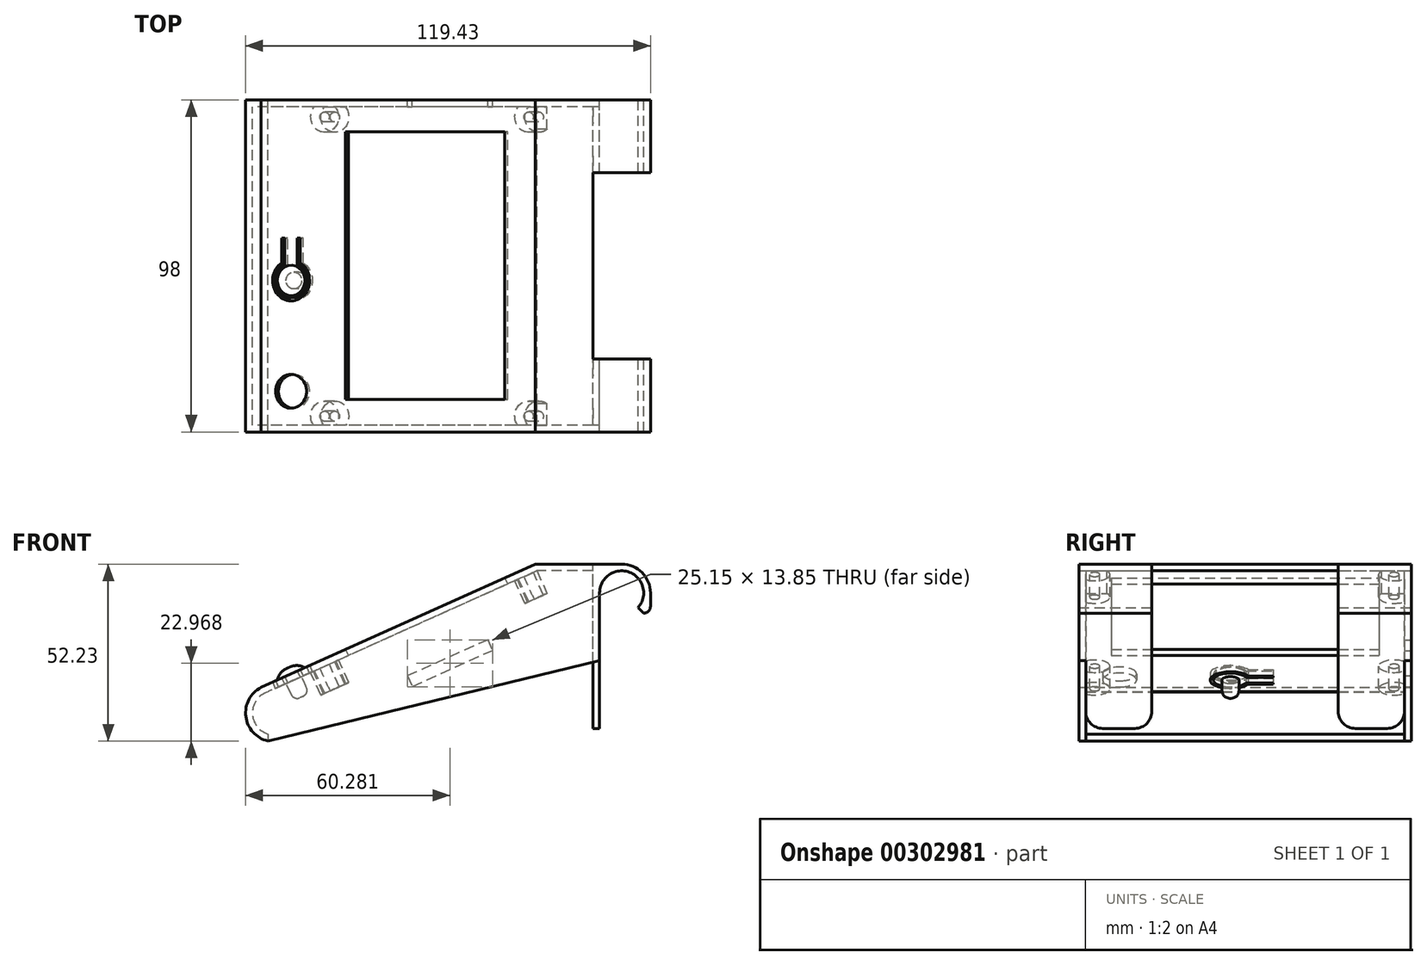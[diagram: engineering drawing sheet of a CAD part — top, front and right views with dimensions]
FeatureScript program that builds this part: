
annotation { "Feature Type Name" : "Feature", "Feature Type Description" : "" }
export const myFeature = defineFeature(function(context is Context, id is Id, definition is map)
    precondition{}
    {
        {
            var Q0;
            Q0=qCreatedBy(makeId("Front.planeOp"),FACE);
            var sketch = newSketch(context, id + "F0", { "sketchPlane" : qUnion([Q0])});
            skLineSegment(sketch, "E0", {"start": v(0, 0) * mm, "end": v(0, -42.85) * mm, "construction": true});
            skLineSegment(sketch, "E1", {"start": v(0, -42.85) * mm, "end": v(-104.35, -42.85) * mm, "construction": true});
            skLineSegment(sketch, "E2", {"start": v(-8.5, 6.5) * mm, "end": v(-25, 6.5) * mm});
            skLineSegment(sketch, "E3", {"start": v(-25, 6.5) * mm, "end": v(-104.35, -29.17) * mm});
            skLineSegment(sketch, "E4", {"start": v(-104.35, -29.17) * mm, "end": v(-104.35, -29.2) * mm});
            skLineSegment(sketch, "E5", {"start": v(-104.35, -29.17) * mm, "end": v(-98.2, -42.85) * mm, "construction": true});
            skLineSegment(sketch, "E6", {"start": v(-25, 6.5) * mm, "end": v(-18.85, -7.18) * mm, "construction": true});
            skLineSegment(sketch, "E7", {"start": v(-6.5, 0) * mm, "end": v(-6.5, -20) * mm});
            skArc(sketch, "E8.0", {"start": v(8.5, 0) * mm, "mid": v(6.01, 6.01) * mm, "end": v(0, 8.5) * mm});
            skLineSegment(sketch, "E9.1", {"start": v(-25.43, 8.5) * mm, "end": v(-106.35, -27.87) * mm});
            skLineSegment(sketch, "E9.2", {"start": v(0, 8.5) * mm, "end": v(-25.43, 8.5) * mm});
            skLineSegment(sketch, "E10", {"start": v(8.5, 0) * mm, "end": v(8.5, -6) * mm});
            skLineSegment(sketch, "E11", {"start": v(8.5, -6) * mm, "end": v(6.5, -6) * mm});
            skLineSegment(sketch, "E12", {"start": v(-8.5, 0) * mm, "end": v(-8.5, -20) * mm});
            skLineSegment(sketch, "E13", {"start": v(-8.5, -20) * mm, "end": v(-6.5, -20) * mm});
            skLineSegment(sketch, "E14", {"start": v(-8.5, 0) * mm, "end": v(-8.5, 6.5) * mm});
            skPoint(sketch, "E15.orphan", {"position": v(0, 6.5) * mm});
            skArc(sketch, "E16", {"start": v(-105.43, -27.46) * mm, "mid": v(-110.9, -36) * mm, "end": v(-104.35, -43.73) * mm});
            skPoint(sketch, "E16.third.point", {"position": v(-95.6, -40.58) * mm});
            skArc(sketch, "E17.0", {"start": v(-104.34, -29.2) * mm, "mid": v(-108.93, -35.42) * mm, "end": v(-104.35, -41.66) * mm});
            skLineSegment(sketch, "E18.trimOffspring", {"start": v(-104.35, -41.66) * mm, "end": v(-104.35, -42.85) * mm});
            skLineSegment(sketch, "E19", {"start": v(-104.35, -42.85) * mm, "end": v(-104.35, -43.73) * mm});
            skArc(sketch, "E20", {"start": v(4.85, -4.33) * mm, "mid": v(2.32, 6.07) * mm, "end": v(-6.5, 0) * mm});
            skLineSegment(sketch, "E21", {"start": v(6.5, -6) * mm, "end": v(4.85, -4.33) * mm});
            skSolve(sketch);
        }
        {
            var Q0;
            Q0=makeQuery(id+"F0.imprint","IMPRINT",FACE,{"disambiguationData":[TD([[makeQuery(id+"F0.imprint","IMPRINT",EDGE,{"derivedFrom":sQuery(id+"F0.wireOp",EDGE,"BKP1fskQ-plHT-HgYq-gCD3-4WAbrrdzwZiy")}),-1.0]])]});
            var Q1;
            Q1=makeQuery(id+"F0.imprint","IMPRINT",FACE,{"disambiguationData":[TD([[makeQuery(id+"F0.imprint","IMPRINT",EDGE,{"derivedFrom":sQuery(id+"F0.wireOp",EDGE,"E2")}),-1.0]])]});
            extrude(context, id + "F1", {"entities" : qUnion([Q0, Q1]), "endBound" : BoundingType.SYMMETRIC, "depth" : 98 * mm, "offsetDistance" : 25 * mm});
        }
        {
            var Q0;
            Q0=makeQuery(id+"F1.opExtrude","SWEPT_FACE",FACE,{"disambiguationData":[OSD([sQuery(id+"F0.wireOp",EDGE,"E3")])]});
            var sketch = newSketch(context, id + "F2", { "sketchPlane" : qUnion([Q0])});
            skLineSegment(sketch, "E22", {"start": v(-20.14, 44.35) * mm, "end": v(-22.79, 44.35) * mm, "construction": true});
            skCircle(sketch, "E23", {"center": v(-22.79, 44.35) * mm, "radius": 1.5 * mm});
            skCircle(sketch, "E24", {"center": v(-22.79, 44.35) * mm, "radius": 4.5 * mm});
            skLineSegment(sketch, "E25", {"start": v(-22.79, 44.35) * mm, "end": v(-22.79, -43.95) * mm, "construction": true});
            skCircle(sketch, "E26", {"center": v(-22.79, -43.95) * mm, "radius": 1.5 * mm});
            skCircle(sketch, "E27", {"center": v(-22.79, -43.95) * mm, "radius": 4.5 * mm});
            skLineSegment(sketch, "E28", {"start": v(-22.79, 44.35) * mm, "end": v(-88.79, 44.35) * mm, "construction": true});
            skCircle(sketch, "E29", {"center": v(-88.79, 44.35) * mm, "radius": 1.5 * mm});
            skCircle(sketch, "E30", {"center": v(-88.79, 44.35) * mm, "radius": 4.5 * mm});
            skLineSegment(sketch, "E31", {"start": v(-88.79, 44.35) * mm, "end": v(-88.79, -43.95) * mm, "construction": true});
            skCircle(sketch, "E32", {"center": v(-88.79, -43.95) * mm, "radius": 1.5 * mm});
            skCircle(sketch, "E33", {"center": v(-88.79, -43.95) * mm, "radius": 4.5 * mm});
            skLineSegment(sketch, "E34", {"start": v(-20.14, 39.4) * mm, "end": v(-29.64, 39.4) * mm, "construction": true});
            skLineSegment(sketch, "E35.bottom", {"start": v(-29.64, 39.4) * mm, "end": v(-81.14, 39.4) * mm});
            skLineSegment(sketch, "E35.top", {"start": v(-29.64, -39.6) * mm, "end": v(-81.14, -39.6) * mm});
            skLineSegment(sketch, "E35.left", {"start": v(-29.64, 39.4) * mm, "end": v(-29.64, -39.6) * mm});
            skLineSegment(sketch, "E35.right", {"start": v(-81.14, 39.4) * mm, "end": v(-81.14, -39.6) * mm});
            skLineSegment(sketch, "E36", {"start": v(-98.75, 49) * mm, "end": v(-98.75, 37) * mm, "construction": true});
            skCircle(sketch, "E37", {"center": v(-98.75, 37) * mm, "radius": 5 * mm});
            skLineSegment(sketch, "E38", {"start": v(-98.75, 37) * mm, "end": v(-98.75, 4.3) * mm, "construction": true});
            skArc(sketch, "E39", {"start": v(-96.75, -0.28) * mm, "mid": v(-98.75, 9.3) * mm, "end": v(-100.75, -0.28) * mm});
            skArc(sketch, "E40", {"start": v(-95.75, -0.9) * mm, "mid": v(-98.75, 10.3) * mm, "end": v(-101.75, -0.9) * mm});
            skLineSegment(sketch, "E41", {"start": v(-98.75, 9.82) * mm, "end": v(-98.75, 4.3) * mm, "construction": true});
            skLineSegment(sketch, "E42", {"start": v(-100.75, -0.28) * mm, "end": v(-100.75, -8.28) * mm});
            skLineSegment(sketch, "E43", {"start": v(-96.75, -0.28) * mm, "end": v(-96.75, -8.28) * mm});
            skLineSegment(sketch, "E44", {"start": v(-101.75, -0.9) * mm, "end": v(-101.75, -8.28) * mm});
            skLineSegment(sketch, "E45", {"start": v(-95.75, -0.9) * mm, "end": v(-95.75, -8.28) * mm});
            skLineSegment(sketch, "E46", {"start": v(-95.75, -8.28) * mm, "end": v(-96.75, -8.28) * mm});
            skLineSegment(sketch, "E47", {"start": v(-100.75, -8.28) * mm, "end": v(-101.75, -8.28) * mm});
            skSolve(sketch);
        }
        {
            var Q0;
            Q0=makeQuery(id+"F2.imprint","IMPRINT",FACE,{"disambiguationData":[TD([[makeQuery(id+"F2.imprint","IMPRINT",EDGE,{"derivedFrom":sQuery(id+"F2.wireOp",EDGE,"FYazuGxI-XyyZ-jJ84-9QZj-pF02LvgmxLtU")}),1.0]])]});
            var Q1;
            Q1=makeQuery(id+"F2.imprint","IMPRINT",FACE,{"disambiguationData":[TD([[makeQuery(id+"F2.imprint","IMPRINT",EDGE,{"derivedFrom":sQuery(id+"F2.wireOp",EDGE,"E35.bottom")}),1.0]])]});
            extrude(context, id + "F3", {"entities" : qUnion([Q0, Q1]), "operationType" : NewBodyOperationType.REMOVE, "oppositeDirection" : true, "depth" : 2 * mm, "offsetDistance" : 25 * mm});
        }
        {
            var Q0;
            Q0=makeQuery(id+"F2.imprint","IMPRINT",FACE,{"disambiguationData":[TD([[makeQuery(id+"F2.imprint","IMPRINT",EDGE,{"derivedFrom":sQuery(id+"F2.wireOp",EDGE,"E23")}),-1.0]])]});
            var Q1;
            Q1=makeQuery(id+"F2.imprint","IMPRINT",FACE,{"disambiguationData":[TD([[makeQuery(id+"F2.imprint","IMPRINT",EDGE,{"derivedFrom":sQuery(id+"F2.wireOp",EDGE,"E26")}),-1.0]])]});
            var Q2;
            Q2=makeQuery(id+"F2.imprint","IMPRINT",FACE,{"disambiguationData":[TD([[makeQuery(id+"F2.imprint","IMPRINT",EDGE,{"derivedFrom":sQuery(id+"F2.wireOp",EDGE,"E32")}),-1.0]])]});
            var Q3;
            Q3=makeQuery(id+"F2.imprint","IMPRINT",FACE,{"disambiguationData":[TD([[makeQuery(id+"F2.imprint","IMPRINT",EDGE,{"derivedFrom":sQuery(id+"F2.wireOp",EDGE,"E29")}),-1.0]])]});
            extrude(context, id + "F4", {"entities" : qUnion([Q0, Q1, Q2, Q3]), "operationType" : NewBodyOperationType.ADD, "depth" : 7.3 * mm, "offsetDistance" : 25 * mm});
        }
        {
            var Q0;
            Q0=makeQuery(id+"F1.opExtrude","CAP_FACE",FACE,{"disambiguationData":[OSD([sQuery(id+"F0.wireOp",EDGE,"BKP1fskQ-plHT-HgYq-gCD3-4WAbrrdzwZiy"),sQuery(id+"F0.wireOp",EDGE,"E2"),sQuery(id+"F0.wireOp",EDGE,"E3"),sQuery(id+"F0.wireOp",EDGE,"E4"),sQuery(id+"F0.wireOp",EDGE,"KLzS8VjV-iBDu-Stew-j29a-tq2aAh7S9TWP"),sQuery(id+"F0.wireOp",EDGE,"E7"),sQuery(id+"F0.wireOp",EDGE,"E8.0"),sQuery(id+"F0.wireOp",EDGE,"E9.1"),sQuery(id+"F0.wireOp",EDGE,"E9.2"),sQuery(id+"F0.wireOp",EDGE,"E10"),sQuery(id+"F0.wireOp",EDGE,"E11"),sQuery(id+"F0.wireOp",EDGE,"E12"),sQuery(id+"F0.wireOp",EDGE,"E13"),sQuery(id+"F0.wireOp",EDGE,"E14"),sQuery(id+"F0.wireOp",EDGE,"E16"),sQuery(id+"F0.wireOp",EDGE,"E17.0"),sQuery(id+"F0.wireOp",EDGE,"E18.trimOffspring"),sQuery(id+"F0.wireOp",EDGE,"E19")])],"isStart":false});
            var sketch = newSketch(context, id + "F5", { "sketchPlane" : qUnion([Q0])});
            skLineSegment(sketch, "E48", {"start": v(-6.5, -20) * mm, "end": v(-104.35, -43.73) * mm});
            skSolve(sketch);
        }
        {
            var Q0;
            Q0=makeQuery(id+"F5.imprint","IMPRINT",FACE,{"disambiguationData":[TD([[makeQuery(id+"F5.imprint","IMPRINT",EDGE,{"derivedFrom":sQuery(id+"F5.wireOp",EDGE,"E48")}),-1.0]])]});
            extrude(context, id + "F6", {"entities" : qUnion([Q0]), "operationType" : NewBodyOperationType.ADD, "oppositeDirection" : true, "depth" : 2 * mm, "offsetDistance" : 25 * mm});
        }
        {
            var Q0;
            Q0=makeQuery(id+"F1.opExtrude","CAP_FACE",FACE,{"disambiguationData":[OSD([sQuery(id+"F0.wireOp",EDGE,"BKP1fskQ-plHT-HgYq-gCD3-4WAbrrdzwZiy"),sQuery(id+"F0.wireOp",EDGE,"E2"),sQuery(id+"F0.wireOp",EDGE,"E3"),sQuery(id+"F0.wireOp",EDGE,"E4"),sQuery(id+"F0.wireOp",EDGE,"KLzS8VjV-iBDu-Stew-j29a-tq2aAh7S9TWP"),sQuery(id+"F0.wireOp",EDGE,"E7"),sQuery(id+"F0.wireOp",EDGE,"E8.0"),sQuery(id+"F0.wireOp",EDGE,"E9.1"),sQuery(id+"F0.wireOp",EDGE,"E9.2"),sQuery(id+"F0.wireOp",EDGE,"E10"),sQuery(id+"F0.wireOp",EDGE,"E11"),sQuery(id+"F0.wireOp",EDGE,"E12"),sQuery(id+"F0.wireOp",EDGE,"E13"),sQuery(id+"F0.wireOp",EDGE,"E14"),sQuery(id+"F0.wireOp",EDGE,"E16"),sQuery(id+"F0.wireOp",EDGE,"E17.0"),sQuery(id+"F0.wireOp",EDGE,"E18.trimOffspring"),sQuery(id+"F0.wireOp",EDGE,"E19")])],"isStart":true});
            var sketch = newSketch(context, id + "F7", { "sketchPlane" : qUnion([Q0])});
            skLineSegment(sketch, "E49", {"start": v(6.5, -20) * mm, "end": v(104.35, -43.73) * mm});
            skSolve(sketch);
        }
        {
            var Q0;
            Q0=makeQuery(id+"F7.imprint","IMPRINT",FACE,{"disambiguationData":[TD([[makeQuery(id+"F7.imprint","IMPRINT",EDGE,{"derivedFrom":sQuery(id+"F7.wireOp",EDGE,"E49")}),1.0]])]});
            extrude(context, id + "F8", {"entities" : qUnion([Q0]), "operationType" : NewBodyOperationType.ADD, "oppositeDirection" : true, "depth" : 2 * mm, "offsetDistance" : 25 * mm});
        }
        {
            var Q0;
            Q0=makeQuery(id+"F2.imprint","IMPRINT",FACE,{"disambiguationData":[TD([[makeQuery(id+"F2.imprint","IMPRINT",EDGE,{"derivedFrom":sQuery(id+"F2.wireOp",EDGE,"E37")}),1.0]])]});
            extrude(context, id + "F9", {"entities" : qUnion([Q0]), "operationType" : NewBodyOperationType.REMOVE, "oppositeDirection" : true, "depth" : 2 * mm, "offsetDistance" : 25 * mm});
        }
        {
            var Q0;
            {var subQ0=sQuery(id+"F0.wireOp",EDGE,"E19");var subQ1=sQuery(id+"F0.wireOp",EDGE,"E18.trimOffspring");var subQ2=sQuery(id+"F0.wireOp",EDGE,"E17.0");var subQ3=sQuery(id+"F0.wireOp",EDGE,"E14");var subQ4=sQuery(id+"F0.wireOp",EDGE,"E13");var subQ5=sQuery(id+"F0.wireOp",EDGE,"E12");var subQ6=sQuery(id+"F0.wireOp",EDGE,"E4");var subQ7=sQuery(id+"F0.wireOp",EDGE,"E3");var subQ8=sQuery(id+"F0.wireOp",EDGE,"E2");Q0=makeQuery(id+"F8.boolean.opBoolean","MERGE",FACE,{"derivedFrom":[makeQuery(id+"F1.opExtrude","CAP_FACE",FACE,{"disambiguationData":[OSD([sQuery(id+"F0.wireOp",EDGE,"BKP1fskQ-plHT-HgYq-gCD3-4WAbrrdzwZiy"),subQ8,subQ7,subQ6,sQuery(id+"F0.wireOp",EDGE,"KLzS8VjV-iBDu-Stew-j29a-tq2aAh7S9TWP"),sQuery(id+"F0.wireOp",EDGE,"E7"),sQuery(id+"F0.wireOp",EDGE,"E8.0"),sQuery(id+"F0.wireOp",EDGE,"E9.1"),sQuery(id+"F0.wireOp",EDGE,"E9.2"),sQuery(id+"F0.wireOp",EDGE,"E10"),sQuery(id+"F0.wireOp",EDGE,"E11"),subQ5,subQ4,subQ3,sQuery(id+"F0.wireOp",EDGE,"E16"),subQ2,subQ1,subQ0])],"isStart":true}),makeQuery(id+"F8.opExtrude","CAP_FACE",FACE,{"disambiguationData":[OSD([subQ8,subQ7,subQ6,subQ5,subQ4,subQ3,subQ2,subQ1,subQ0,sQuery(id+"F7.wireOp",EDGE,"E49")])],"isStart":true})]});}
            var sketch = newSketch(context, id + "F10", { "sketchPlane" : qUnion([Q0])});
            skLineSegment(sketch, "E50", {"start": v(25.43, 8.5) * mm, "end": v(19.44, -4.82) * mm, "construction": true});
            skLineSegment(sketch, "E51", {"start": v(19.44, -4.82) * mm, "end": v(39.5, -13.84) * mm, "construction": true});
            skLineSegment(sketch, "E52", {"start": v(39.5, -13.84) * mm, "end": v(63.22, -24.5) * mm});
            skLineSegment(sketch, "E53.0", {"start": v(38.07, -17.03) * mm, "end": v(61.79, -27.69) * mm});
            skLineSegment(sketch, "E54", {"start": v(39.5, -13.84) * mm, "end": v(38.07, -17.03) * mm});
            skLineSegment(sketch, "E55", {"start": v(63.22, -24.5) * mm, "end": v(61.79, -27.69) * mm});
            skSolve(sketch);
        }
        {
            var Q0;
            Q0=makeQuery(id+"F10.imprint","IMPRINT",FACE,{"disambiguationData":[TD([[makeQuery(id+"F10.imprint","IMPRINT",EDGE,{"derivedFrom":sQuery(id+"F10.wireOp",EDGE,"E52")}),-1.0]])]});
            extrude(context, id + "F11", {"entities" : qUnion([Q0]), "operationType" : NewBodyOperationType.REMOVE, "oppositeDirection" : true, "depth" : 2 * mm, "offsetDistance" : 25 * mm});
        }
        {
            var Q0;
            Q0=makeQuery(id+"F1.opExtrude","SWEPT_FACE",FACE,{"disambiguationData":[OSD([sQuery(id+"F0.wireOp",EDGE,"E9.2")])]});
            var sketch = newSketch(context, id + "F12", { "sketchPlane" : qUnion([Q0])});
            skLineSegment(sketch, "E56.bottom", {"start": v(8.5, 27.5) * mm, "end": v(-8.5, 27.5) * mm});
            skLineSegment(sketch, "E56.top", {"start": v(8.5, -27.5) * mm, "end": v(-8.5, -27.5) * mm});
            skLineSegment(sketch, "E56.left", {"start": v(8.5, 27.5) * mm, "end": v(8.5, -27.5) * mm});
            skLineSegment(sketch, "E56.right", {"start": v(-8.5, 27.5) * mm, "end": v(-8.5, -27.5) * mm});
            skPoint(sketch, "E56.middle", {"position": v(0, 0) * mm});
            skSolve(sketch);
        }
        {
            var Q0;
            {var subQ0=sQuery(id+"F12.wireOp",EDGE,"E56.left");Q0=makeQuery(id+"F12.imprint","IMPRINT",FACE,{"disambiguationData":[TD([[makeQuery(id+"F12.imprint","IMPRINT",EDGE,{"derivedFrom":subQ0}),-1.0]])]});}
            var Q1;
            {var subQ0=sQuery(id+"F12.wireOp",EDGE,"E56.right");Q1=makeQuery(id+"F12.imprint","IMPRINT",FACE,{"disambiguationData":[TD([[makeQuery(id+"F12.imprint","IMPRINT",EDGE,{"derivedFrom":subQ0}),1.0]])]});}
            extrude(context, id + "F13", {"entities" : qUnion([Q0, Q1]), "operationType" : NewBodyOperationType.REMOVE, "oppositeDirection" : true, "depth" : 40 * mm, "offsetDistance" : 25 * mm});
        }
        {
            var Q0;
            {var subQ0=sQuery(id+"F0.wireOp",EDGE,"E11");var subQ10=sQuery(id+"F0.wireOp",EDGE,"E10");Q0=makeQuery(id+"F13.boolean.opBoolean","SPLIT",EDGE,{"disambiguationData":[TD([makeQuery(id+"F13.opExtrude","SWEPT_FACE",FACE,{"disambiguationData":[OSD([sQuery(id+"F12.wireOp",EDGE,"E56.bottom")])]})])],"derivedFrom":makeQuery(id+"F1.opExtrude","SWEPT_EDGE",EDGE,{"disambiguationData":[OSD([subQ10,subQ0])]})});}
            var Q1;
            {var subQ9=sQuery(id+"F0.wireOp",EDGE,"E11");var subQ10=sQuery(id+"F0.wireOp",EDGE,"E10");Q1=makeQuery(id+"F13.boolean.opBoolean","SPLIT",EDGE,{"disambiguationData":[TD([makeQuery(id+"F13.opExtrude","SWEPT_FACE",FACE,{"disambiguationData":[OSD([sQuery(id+"F12.wireOp",EDGE,"E56.top")])]})])],"derivedFrom":makeQuery(id+"F1.opExtrude","SWEPT_EDGE",EDGE,{"disambiguationData":[OSD([subQ10,subQ9])]})});}
            fillet(context, id + "F14", {"entities" : qUnion([Q0, Q1]), "radius" : 2 * mm, "tangentPropagation" : true, "allowEdgeOverflow" : false});
        }
        {
            var Q0;
            {var subQ0=sQuery(id+"F5.wireOp",EDGE,"E48");var subQ2=sQuery(id+"F0.wireOp",EDGE,"E13");Q0=makeQuery(id+"F13.boolean.opBoolean","SPLIT",FACE,{"disambiguationData":[TD([makeQuery(id+"F6.opExtrude","SWEPT_FACE",FACE,{"disambiguationData":[OSD([subQ0])]})])],"derivedFrom":makeQuery(id+"F1.opExtrude","SWEPT_FACE",FACE,{"disambiguationData":[OSD([subQ2])]})});}
            var sketch = newSketch(context, id + "F15", { "sketchPlane" : qUnion([Q0])});
            skLineSegment(sketch, "E57.bottom", {"start": v(-6.5, 27.5) * mm, "end": v(-8.5, 27.5) * mm});
            skLineSegment(sketch, "E57.top", {"start": v(-6.5, 47) * mm, "end": v(-8.5, 47) * mm});
            skLineSegment(sketch, "E57.left", {"start": v(-6.5, 27.5) * mm, "end": v(-6.5, 47) * mm});
            skLineSegment(sketch, "E57.right", {"start": v(-8.5, 27.5) * mm, "end": v(-8.5, 47) * mm});
            skSolve(sketch);
        }
        {
            var Q0;
            Q0=makeQuery(id+"F15.imprint","IMPRINT",FACE,{"disambiguationData":[TD([[makeQuery(id+"F15.imprint","IMPRINT",EDGE,{"derivedFrom":sQuery(id+"F15.wireOp",EDGE,"E57.bottom")}),-1.0]])]});
            extrude(context, id + "F16", {"entities" : qUnion([Q0]), "operationType" : NewBodyOperationType.ADD, "depth" : 20 * mm, "offsetDistance" : 25 * mm});
        }
        {
            var Q0;
            {var subQ0=sQuery(id+"F7.wireOp",EDGE,"E49");var subQ3=sQuery(id+"F0.wireOp",EDGE,"E13");Q0=makeQuery(id+"F13.boolean.opBoolean","SPLIT",FACE,{"disambiguationData":[TD([makeQuery(id+"F8.opExtrude","SWEPT_FACE",FACE,{"disambiguationData":[OSD([subQ0])]})])],"derivedFrom":makeQuery(id+"F1.opExtrude","SWEPT_FACE",FACE,{"disambiguationData":[OSD([subQ3])]})});}
            var sketch = newSketch(context, id + "F17", { "sketchPlane" : qUnion([Q0])});
            skLineSegment(sketch, "E58.bottom", {"start": v(-6.5, -27.5) * mm, "end": v(-8.5, -27.5) * mm});
            skLineSegment(sketch, "E58.top", {"start": v(-6.5, -47) * mm, "end": v(-8.5, -47) * mm});
            skLineSegment(sketch, "E58.left", {"start": v(-6.5, -27.5) * mm, "end": v(-6.5, -47) * mm});
            skLineSegment(sketch, "E58.right", {"start": v(-8.5, -27.5) * mm, "end": v(-8.5, -47) * mm});
            skSolve(sketch);
        }
        {
            var Q0;
            Q0=makeQuery(id+"F17.imprint","IMPRINT",FACE,{"disambiguationData":[TD([[makeQuery(id+"F17.imprint","IMPRINT",EDGE,{"derivedFrom":sQuery(id+"F17.wireOp",EDGE,"E58.bottom")}),1.0]])]});
            extrude(context, id + "F18", {"entities" : qUnion([Q0]), "operationType" : NewBodyOperationType.ADD, "depth" : 20 * mm, "offsetDistance" : 25 * mm});
        }
        {
            var Q0;
            Q0=makeQuery(id+"F18.opExtrude","CAP_EDGE",EDGE,{"disambiguationData":[OSD([sQuery(id+"F17.wireOp",EDGE,"E58.top")])],"isStart":false});
            var Q1;
            Q1=makeQuery(id+"F18.opExtrude","CAP_EDGE",EDGE,{"disambiguationData":[OSD([sQuery(id+"F17.wireOp",EDGE,"E58.bottom")])],"isStart":false});
            var Q2;
            Q2=makeQuery(id+"F16.opExtrude","CAP_EDGE",EDGE,{"disambiguationData":[OSD([sQuery(id+"F15.wireOp",EDGE,"E57.bottom")])],"isStart":false});
            var Q3;
            Q3=makeQuery(id+"F16.opExtrude","CAP_EDGE",EDGE,{"disambiguationData":[OSD([sQuery(id+"F15.wireOp",EDGE,"E57.top")])],"isStart":false});
            fillet(context, id + "F19", {"entities" : qUnion([Q0, Q1, Q2, Q3]), "radius" : 5 * mm, "tangentPropagation" : true, "allowEdgeOverflow" : false});
        }
        {
            var Q0;
            Q0=makeQuery(id+"F2.imprint","IMPRINT",FACE,{"disambiguationData":[TD([[makeQuery(id+"F2.imprint","IMPRINT",EDGE,{"derivedFrom":sQuery(id+"F2.wireOp",EDGE,"E39")}),-1.0]])]});
            extrude(context, id + "F20", {"entities" : qUnion([Q0]), "operationType" : NewBodyOperationType.REMOVE, "oppositeDirection" : true, "depth" : 2 * mm, "offsetDistance" : 25 * mm});
        }
        {
            var Q0;
            Q0=makeQuery(id+"F1.opExtrude","SWEPT_FACE",FACE,{"disambiguationData":[OSD([sQuery(id+"F0.wireOp",EDGE,"E9.1")])]});
            var sketch = newSketch(context, id + "F21", { "sketchPlane" : qUnion([Q0])});
            skCircle(sketch, "E59", {"center": v(-98.75, -4.3) * mm, "radius": 4.5 * mm});
            skCircle(sketch, "E60", {"center": v(-98.75, -4.3) * mm, "radius": 2.5 * mm});
            skSolve(sketch);
        }
        {
            var Q0;
            Q0=makeQuery(id+"F21.imprint","IMPRINT",FACE,{"disambiguationData":[TD([[makeQuery(id+"F21.imprint","IMPRINT",EDGE,{"derivedFrom":sQuery(id+"F21.wireOp",EDGE,"E60")}),1.0]])]});
            extrude(context, id + "F22", {"entities" : qUnion([Q0]), "operationType" : NewBodyOperationType.ADD, "oppositeDirection" : true, "depth" : 7.5 * mm, "offsetDistance" : 25 * mm});
        }
        {
            var Q0;
            Q0=makeQuery(id+"F21.imprint","IMPRINT",FACE,{"disambiguationData":[TD([[makeQuery(id+"F21.imprint","IMPRINT",EDGE,{"derivedFrom":sQuery(id+"F21.wireOp",EDGE,"E60")}),1.0]])]});
            var Q1;
            Q1=makeQuery(id+"F21.imprint","IMPRINT",FACE,{"disambiguationData":[TD([[makeQuery(id+"F21.imprint","IMPRINT",EDGE,{"derivedFrom":sQuery(id+"F21.wireOp",EDGE,"E59")}),1.0]])]});
            extrude(context, id + "F23", {"entities" : qUnion([Q0, Q1]), "operationType" : NewBodyOperationType.ADD, "depth" : 2 * mm, "offsetDistance" : 25 * mm});
        }
        {
            var Q0;
            Q0=makeQuery(id+"F23.opExtrude","CAP_EDGE",EDGE,{"disambiguationData":[OSD([sQuery(id+"F21.wireOp",EDGE,"E59")])],"isStart":false});
            fillet(context, id + "F24", {"entities" : qUnion([Q0]), "radius" : 5 * mm, "tangentPropagation" : true, "allowEdgeOverflow" : false});
        }
        {
            var Q0;
            Q0=makeQuery(id+"F22.opExtrude","CAP_EDGE",EDGE,{"disambiguationData":[OSD([sQuery(id+"F21.wireOp",EDGE,"E60")])],"isStart":false});
            fillet(context, id + "F25", {"entities" : qUnion([Q0]), "radius" : 2 * mm, "tangentPropagation" : true, "allowEdgeOverflow" : false});
        }
    });
